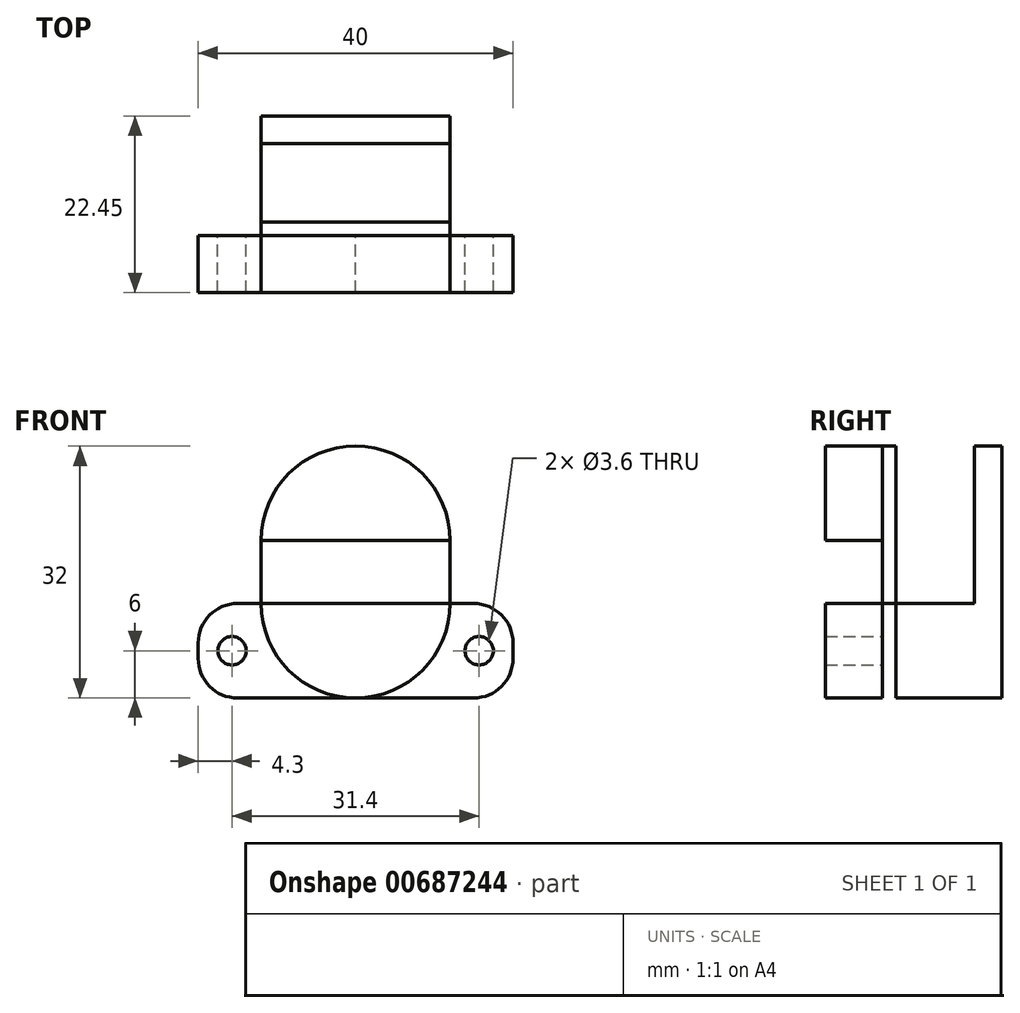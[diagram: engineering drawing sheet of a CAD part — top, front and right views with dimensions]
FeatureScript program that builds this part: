
annotation { "Feature Type Name" : "Feature", "Feature Type Description" : "" }
export const myFeature = defineFeature(function(context is Context, id is Id, definition is map)
    precondition{}
    {
        {
            var Q0;
            Q0=qCreatedBy(makeId("Front.planeOp"),FACE);
            var sketch = newSketch(context, id + "F0", { "sketchPlane" : qUnion([Q0])});
            skLineSegment(sketch, "E0.bottom", {"start": v(-20, 12) * mm, "end": v(20, 12) * mm});
            skLineSegment(sketch, "E0.top", {"start": v(-20, 0) * mm, "end": v(20, 0) * mm});
            skLineSegment(sketch, "E0.left", {"start": v(-20, 12) * mm, "end": v(-20, 0) * mm});
            skLineSegment(sketch, "E0.right", {"start": v(20, 12) * mm, "end": v(20, 0) * mm});
            skLineSegment(sketch, "E1", {"start": v(0, 20.86) * mm, "end": v(0, -29.6) * mm, "construction": true});
            skLineSegment(sketch, "E2", {"start": v(-12, 20) * mm, "end": v(12, 20) * mm});
            skArc(sketch, "E3", {"start": v(12, 20) * mm, "mid": v(0, 32) * mm, "end": v(-12, 20) * mm});
            skPoint(sketch, "E3.third.point", {"position": v(0, 32) * mm});
            skPoint(sketch, "E4.MirrorP", {"position": v(0, -26) * mm});
            skLineSegment(sketch, "E5", {"start": v(-12, 20) * mm, "end": v(-12, 12) * mm});
            skLineSegment(sketch, "E6", {"start": v(12, 20) * mm, "end": v(12, 12) * mm});
            skLineSegment(sketch, "E7", {"start": v(-31.4, 16) * mm, "end": v(45.65, 16) * mm, "construction": true});
            skLineSegment(sketch, "E8.MirrorCS", {"start": v(-12, 12) * mm, "end": v(12, 12) * mm});
            skArc(sketch, "E9.MirrorCS", {"start": v(12, 12) * mm, "mid": v(0, 0) * mm, "end": v(-12, 12) * mm});
            skSolve(sketch);
        }
        {
            var Q0;
            {var subQ0=sQuery(id+"F0.wireOp",EDGE,"E0.right");Q0=makeQuery(id+"F0.imprint","IMPRINT",FACE,{"disambiguationData":[TD([[makeQuery(id+"F0.imprint","IMPRINT",EDGE,{"derivedFrom":subQ0}),-1.0]])]});}
            var Q1;
            {var subQ0=sQuery(id+"F0.wireOp",EDGE,"E8.MirrorCS");Q1=makeQuery(id+"F0.imprint","IMPRINT",FACE,{"disambiguationData":[TD([[makeQuery(id+"F0.imprint","IMPRINT",EDGE,{"derivedFrom":subQ0}),-1.0]])]});}
            var Q2;
            {var subQ0=sQuery(id+"F0.wireOp",EDGE,"E0.left");Q2=makeQuery(id+"F0.imprint","IMPRINT",FACE,{"disambiguationData":[TD([[makeQuery(id+"F0.imprint","IMPRINT",EDGE,{"derivedFrom":subQ0}),1.0]])]});}
            var Q3;
            Q3=makeQuery(id+"F0.imprint","IMPRINT",FACE,{"disambiguationData":[TD([[makeQuery(id+"F0.imprint","IMPRINT",EDGE,{"derivedFrom":sQuery(id+"F0.wireOp",EDGE,"E2")}),1.0]])]});
            extrude(context, id + "F1", {"entities" : qUnion([Q0, Q1, Q2, Q3]), "depth" : 7.25 * mm, "offsetDistance" : 25 * mm});
        }
        {
            var Q0;
            Q0=makeQuery(id+"F0.imprint","IMPRINT",FACE,{"disambiguationData":[TD([[makeQuery(id+"F0.imprint","IMPRINT",EDGE,{"derivedFrom":sQuery(id+"F0.wireOp",EDGE,"E2")}),1.0]])]});
            var Q1;
            Q1=makeQuery(id+"F0.imprint","IMPRINT",FACE,{"disambiguationData":[TD([[makeQuery(id+"F0.imprint","IMPRINT",EDGE,{"derivedFrom":sQuery(id+"F0.wireOp",EDGE,"E2")}),-1.0]])]});
            var Q2;
            {var subQ0=sQuery(id+"F0.wireOp",EDGE,"E8.MirrorCS");Q2=makeQuery(id+"F0.imprint","IMPRINT",FACE,{"disambiguationData":[TD([[makeQuery(id+"F0.imprint","IMPRINT",EDGE,{"derivedFrom":subQ0}),-1.0]])]});}
            extrude(context, id + "F2", {"entities" : qUnion([Q0, Q1, Q2]), "oppositeDirection" : true, "depth" : 1.7 * mm, "offsetDistance" : 25 * mm});
        }
        {
            var Q0;
            Q0=makeQuery(id+"F2.opExtrude","CAP_FACE",FACE,{"disambiguationData":[OSD([sQuery(id+"F0.wireOp",EDGE,"E3"),sQuery(id+"F0.wireOp",EDGE,"E5"),sQuery(id+"F0.wireOp",EDGE,"E6"),sQuery(id+"F0.wireOp",EDGE,"E9.MirrorCS")])],"isStart":false});
            var sketch = newSketch(context, id + "F3", { "sketchPlane" : qUnion([Q0])});
            skLineSegment(sketch, "E10.0", {"start": v(12, 12) * mm, "end": v(-12, 12) * mm});
            skArc(sketch, "E10.1", {"start": v(-12, 12) * mm, "mid": v(0, 0) * mm, "end": v(12, 12) * mm});
            skSolve(sketch);
        }
        {
            var Q0;
            Q0 = qSketchRegion(id + "F3", true);
            extrude(context, id + "F4", {"entities" : qUnion([Q0]), "operationType" : NewBodyOperationType.ADD, "depth" : 10 * mm, "offsetDistance" : 25 * mm});
        }
        {
            var Q0;
            Q0=makeQuery(id+"F4.opExtrude","CAP_FACE",FACE,{"disambiguationData":[OSD([sQuery(id+"F3.wireOp",EDGE,"E10.0"),sQuery(id+"F3.wireOp",EDGE,"E10.1")])],"isStart":false});
            var sketch = newSketch(context, id + "F5", { "sketchPlane" : qUnion([Q0])});
            skLineSegment(sketch, "E11.0", {"start": v(-12, 20) * mm, "end": v(-12, 12) * mm});
            skLineSegment(sketch, "E11.1", {"start": v(12, 20) * mm, "end": v(12, 12) * mm});
            skArc(sketch, "E11.2", {"start": v(-12, 20) * mm, "mid": v(0, 32) * mm, "end": v(12, 20) * mm});
            skArc(sketch, "E11.3", {"start": v(-12, 12) * mm, "mid": v(0, 0) * mm, "end": v(12, 12) * mm});
            skSolve(sketch);
        }
        {
            var Q0;
            Q0 = qSketchRegion(id + "F5", true);
            extrude(context, id + "F6", {"entities" : qUnion([Q0]), "operationType" : NewBodyOperationType.ADD, "depth" : 3.5 * mm, "offsetDistance" : 25 * mm});
        }
        {
            var Q0;
            Q0=makeQuery(id+"F1.opExtrude","SWEPT_EDGE",EDGE,{"disambiguationData":[OSD([sQuery(id+"F0.wireOp",EDGE,"E0.bottom"),sQuery(id+"F0.wireOp",EDGE,"E0.left")])]});
            var Q1;
            Q1=makeQuery(id+"F1.opExtrude","SWEPT_EDGE",EDGE,{"disambiguationData":[OSD([sQuery(id+"F0.wireOp",EDGE,"E0.top"),sQuery(id+"F0.wireOp",EDGE,"E0.left")])]});
            var Q2;
            Q2=makeQuery(id+"F1.opExtrude","SWEPT_EDGE",EDGE,{"disambiguationData":[OSD([sQuery(id+"F0.wireOp",EDGE,"E0.bottom"),sQuery(id+"F0.wireOp",EDGE,"E0.right")])]});
            var Q3;
            Q3=makeQuery(id+"F1.opExtrude","SWEPT_EDGE",EDGE,{"disambiguationData":[OSD([sQuery(id+"F0.wireOp",EDGE,"E0.top"),sQuery(id+"F0.wireOp",EDGE,"E0.right")])]});
            fillet(context, id + "F7", {"entities" : qUnion([Q0, Q1, Q2, Q3]), "radius" : 5 * mm, "tangentPropagation" : true, "allowEdgeOverflow" : false});
        }
        {
            var Q0;
            {var subQ0=sQuery(id+"F0.wireOp",EDGE,"E0.right");Q0=makeQuery(id+"F0.imprint","IMPRINT",FACE,{"disambiguationData":[TD([[makeQuery(id+"F0.imprint","IMPRINT",EDGE,{"derivedFrom":subQ0}),-1.0]])]});}
            var sketch = newSketch(context, id + "F8", { "sketchPlane" : qUnion([Q0])});
            skCircle(sketch, "E12", {"center": v(15.7, 6) * mm, "radius": 1.8 * mm});
            skCircle(sketch, "E13.MirrorC", {"center": v(-15.7, 6) * mm, "radius": 1.8 * mm});
            skLineSegment(sketch, "E14", {"start": v(17.5, 10.05) * mm, "end": v(17.5, -2.1) * mm, "construction": true});
            skLineSegment(sketch, "E15.MirrorCS", {"start": v(-17.5, 10.05) * mm, "end": v(-17.5, -2.1) * mm, "construction": true});
            skLineSegment(sketch, "E16", {"start": v(-21.54, 6) * mm, "end": v(20.26, 6) * mm, "construction": true});
            skSolve(sketch);
        }
        {
            var Q0;
            Q0=sQuery(id+"F8.wireOp",VERTEX,"E12.center");
            var Q1;
            Q1=sQuery(id+"F8.wireOp",VERTEX,"E13.MirrorC.center");
            var Q2;
            Q2=makeQuery(id+"F1.opExtrude","SWEPT_BODY",BODY,{"disambiguationData":[OSD([sQuery(id+"F0.wireOp",EDGE,"E0.bottom"),sQuery(id+"F0.wireOp",EDGE,"E0.top"),sQuery(id+"F0.wireOp",EDGE,"E0.left"),sQuery(id+"F0.wireOp",EDGE,"E0.right"),sQuery(id+"F0.wireOp",EDGE,"E8.MirrorCS")])]});
            hole(context, id + "F9", {"style" : HoleStyle.SIMPLE, "endStyle" : HoleEndStyle.THROUGH, "oppositeDirection" : true, "holeDiameter" : 3.6 * mm, "majorDiameter" : 5 * mm, "isTappedThrough" : true, "tappedDepth" : 12 * mm, "tapClearance" : 3, "locations" : qUnion([Q0, Q1]), "scope" : qUnion([Q2])});
        }
    });
